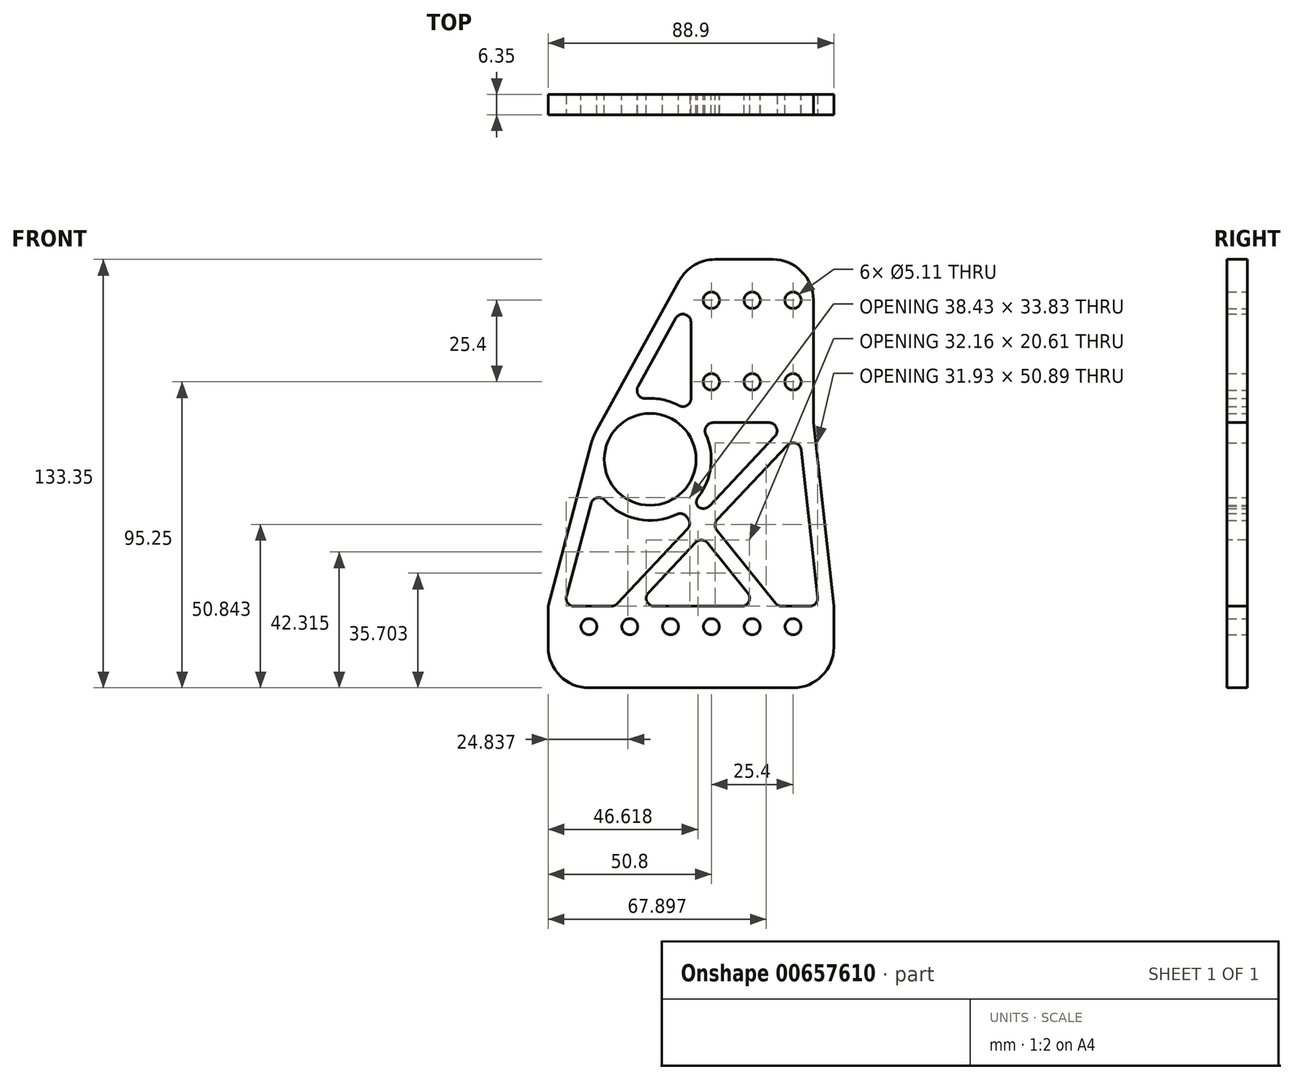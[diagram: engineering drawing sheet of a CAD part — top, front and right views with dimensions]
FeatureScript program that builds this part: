
annotation { "Feature Type Name" : "Feature", "Feature Type Description" : "" }
export const myFeature = defineFeature(function(context is Context, id is Id, definition is map)
    precondition{}
    {
        {
            var Q0;
            Q0=qCreatedBy(makeId("Front.planeOp"),FACE);
            var sketch = newSketch(context, id + "F0", { "sketchPlane" : qUnion([Q0])});
            skLineSegment(sketch, "E0.bottom", {"start": v(0, 0) * mm, "end": v(-88.9, 0) * mm});
            skLineSegment(sketch, "E0.top", {"start": v(0, -152.4) * mm, "end": v(-88.9, -152.4) * mm});
            skLineSegment(sketch, "E0.left", {"start": v(0, 0) * mm, "end": v(0, -152.4) * mm});
            skLineSegment(sketch, "E0.right", {"start": v(-88.9, 0) * mm, "end": v(-88.9, -152.4) * mm});
            skCircle(sketch, "E1", {"center": v(-12.7, -31.75) * mm, "radius": 2.55 * mm});
            skCircle(sketch, "E2", {"center": v(-57.15, -81.28) * mm, "radius": 14.29 * mm});
            skCircle(sketch, "E3.0.1.0", {"center": v(-12.7, -57.15) * mm, "radius": 2.55 * mm});
            skCircle(sketch, "E3.1.0.0", {"center": v(-25.4, -31.75) * mm, "radius": 2.55 * mm});
            skCircle(sketch, "E3.1.1.0", {"center": v(-25.4, -57.15) * mm, "radius": 2.55 * mm});
            skCircle(sketch, "E3.2.0.0", {"center": v(-38.1, -31.75) * mm, "radius": 2.55 * mm});
            skCircle(sketch, "E3.2.1.0", {"center": v(-38.1, -57.15) * mm, "radius": 2.55 * mm});
            skLineSegment(sketch, "E3.direction1", {"start": v(-12.7, -31.75) * mm, "end": v(-25.4, -31.75) * mm, "construction": true});
            skLineSegment(sketch, "E3.direction2", {"start": v(-12.7, -31.75) * mm, "end": v(-12.7, -57.15) * mm, "construction": true});
            skCircle(sketch, "E4", {"center": v(-57.15, -81.28) * mm, "radius": 18.99 * mm});
            skLineSegment(sketch, "E5", {"start": v(-88.9, -127) * mm, "end": v(0, -127) * mm});
            skLineSegment(sketch, "E6", {"start": v(-88.9, -127) * mm, "end": v(-75.5, -76.42) * mm});
            skLineSegment(sketch, "E7", {"start": v(-74.16, -89.7) * mm, "end": v(-84.04, -127) * mm});
            skLineSegment(sketch, "E8", {"start": v(0, -19.05) * mm, "end": v(-44.45, -19.05) * mm});
            skLineSegment(sketch, "E9", {"start": v(-44.45, -19.05) * mm, "end": v(-44.45, -69.85) * mm});
            skLineSegment(sketch, "E10", {"start": v(-44.45, -69.85) * mm, "end": v(0, -69.85) * mm});
            skPoint(sketch, "E11", {"position": v(-25.4, -44.45) * mm});
            skLineSegment(sketch, "E12", {"start": v(-44.45, -19.05) * mm, "end": v(-73.77, -72.1) * mm});
            skLineSegment(sketch, "E13", {"start": v(-44.45, -28.76) * mm, "end": v(-63.6, -63.42) * mm});
            skLineSegment(sketch, "E14", {"start": v(-6.35, -19.05) * mm, "end": v(-6.35, -69.85) * mm});
            skLineSegment(sketch, "E15", {"start": v(-6.35, -69.85) * mm, "end": v(0, -127) * mm});
            skLineSegment(sketch, "E16", {"start": v(-4.73, -127) * mm, "end": v(-11.08, -69.85) * mm});
            skLineSegment(sketch, "E17", {"start": v(-57.15, -81.28) * mm, "end": v(-25.4, -44.45) * mm, "construction": true});
            skLineSegment(sketch, "E18", {"start": v(-46.63, -65.48) * mm, "end": v(-44.45, -62.95) * mm});
            skLineSegment(sketch, "E19", {"start": v(-44.45, -70.15) * mm, "end": v(-43.07, -68.54) * mm});
            skLineSegment(sketch, "E20", {"start": v(-57.15, -81.28) * mm, "end": v(0, -152.4) * mm, "construction": true});
            skLineSegment(sketch, "E21", {"start": v(-47.18, -97.44) * mm, "end": v(-43.52, -94.5) * mm, "construction": true});
            skLineSegment(sketch, "E22", {"start": v(-43.52, -94.5) * mm, "end": v(-17.4, -127) * mm});
            skLineSegment(sketch, "E23", {"start": v(-47.18, -97.44) * mm, "end": v(-23.42, -127) * mm});
            skLineSegment(sketch, "E24", {"start": v(-88.9, -152.4) * mm, "end": v(-11.08, -69.85) * mm, "construction": true});
            skLineSegment(sketch, "E25", {"start": v(-61.73, -127) * mm, "end": v(-10.74, -72.91) * mm});
            skLineSegment(sketch, "E26", {"start": v(-14.3, -69.85) * mm, "end": v(-68.18, -127) * mm});
            skCircle(sketch, "E27", {"center": v(-76.2, -133.35) * mm, "radius": 2.49 * mm});
            skCircle(sketch, "E28.1.0.0", {"center": v(-63.5, -133.35) * mm, "radius": 2.49 * mm});
            skCircle(sketch, "E28.2.0.0", {"center": v(-50.8, -133.35) * mm, "radius": 2.49 * mm});
            skCircle(sketch, "E28.3.0.0", {"center": v(-38.1, -133.35) * mm, "radius": 2.49 * mm});
            skCircle(sketch, "E28.4.0.0", {"center": v(-25.4, -133.35) * mm, "radius": 2.49 * mm});
            skCircle(sketch, "E28.5.0.0", {"center": v(-12.7, -133.35) * mm, "radius": 2.49 * mm});
            skLineSegment(sketch, "E28.direction1", {"start": v(-76.2, -133.35) * mm, "end": v(-63.5, -133.35) * mm, "construction": true});
            skSolve(sketch);
        }
        {
            var Q0;
            Q0=makeQuery(id+"F0.imprint","IMPRINT",FACE,{"disambiguationData":[TD([[makeQuery(id+"F0.imprint","IMPRINT",EDGE,{"derivedFrom":sQuery(id+"F0.wireOp",EDGE,"E2")}),-1.0]])]});
            var Q1;
            {var subQ0=sQuery(id+"F0.wireOp",EDGE,"E12");Q1=makeQuery(id+"F0.imprint","IMPRINT",FACE,{"disambiguationData":[TD([[makeQuery(id+"F0.imprint","IMPRINT",EDGE,{"derivedFrom":subQ0}),1.0]])]});}
            var Q2;
            {var subQ0=sQuery(id+"F0.wireOp",EDGE,"E6");Q2=makeQuery(id+"F0.imprint","IMPRINT",FACE,{"disambiguationData":[TD([[makeQuery(id+"F0.imprint","IMPRINT",EDGE,{"derivedFrom":subQ0}),-1.0]])]});}
            var Q3;
            {var subQ4=sQuery(id+"F0.wireOp",EDGE,"E0.top");Q3=makeQuery(id+"F0.imprint","IMPRINT",FACE,{"disambiguationData":[TD([[makeQuery(id+"F0.imprint","IMPRINT",EDGE,{"derivedFrom":subQ4}),-1.0]])]});}
            var Q4;
            {var subQ0=sQuery(id+"F0.wireOp",EDGE,"E15");Q4=makeQuery(id+"F0.imprint","IMPRINT",FACE,{"disambiguationData":[TD([[makeQuery(id+"F0.imprint","IMPRINT",EDGE,{"derivedFrom":subQ0}),-1.0]])]});}
            var Q5;
            Q5=makeQuery(id+"F0.imprint","IMPRINT",FACE,{"disambiguationData":[TD([[makeQuery(id+"F0.imprint","IMPRINT",EDGE,{"derivedFrom":sQuery(id+"F0.wireOp",EDGE,"E1")}),-1.0]])]});
            var Q6;
            {var subQ0=sQuery(id+"F0.wireOp",EDGE,"E25");var subQ1=sQuery(id+"F0.wireOp",EDGE,"E5");var subQ2=makeQuery(id+"F0.imprint","INTERSECT",VERTEX,{"derivedFrom":[subQ1,subQ0]});Q6=makeQuery(id+"F0.imprint","IMPRINT",FACE,{"disambiguationData":[TD([[makeQuery(id+"F0.imprint","IMPRINT",EDGE,{"disambiguationData":[TD([[subQ2,1.0]])],"derivedFrom":subQ1}),1.0]])]});}
            var Q7;
            {var subQ0=sQuery(id+"F0.wireOp",EDGE,"E26");var subQ1=sQuery(id+"F0.wireOp",EDGE,"E22");var subQ2=makeQuery(id+"F0.imprint","INTERSECT",VERTEX,{"derivedFrom":[subQ1,subQ0]});Q7=makeQuery(id+"F0.imprint","IMPRINT",FACE,{"disambiguationData":[TD([[makeQuery(id+"F0.imprint","IMPRINT",EDGE,{"disambiguationData":[TD([[subQ2,-1.0]])],"derivedFrom":subQ1}),-1.0]])]});}
            var Q8;
            {var subQ1=sQuery(id+"F0.wireOp",EDGE,"E16");var subQ5=sQuery(id+"F0.wireOp",EDGE,"E10");var subQ6=makeQuery(id+"F0.imprint","INTERSECT",VERTEX,{"derivedFrom":[subQ5,subQ1]});Q8=makeQuery(id+"F0.imprint","IMPRINT",FACE,{"disambiguationData":[TD([[makeQuery(id+"F0.imprint","IMPRINT",EDGE,{"disambiguationData":[TD([[subQ6,1.0]])],"derivedFrom":subQ5}),-1.0]])]});}
            var Q9;
            {var subQ0=sQuery(id+"F0.wireOp",EDGE,"E22");var subQ1=sQuery(id+"F0.wireOp",EDGE,"E4");var subQ2=makeQuery(id+"F0.imprint","INTERSECT",VERTEX,{"derivedFrom":[subQ1,subQ0]});Q9=makeQuery(id+"F0.imprint","IMPRINT",FACE,{"disambiguationData":[TD([[makeQuery(id+"F0.imprint","IMPRINT",EDGE,{"disambiguationData":[TD([[subQ2,1.0]])],"derivedFrom":subQ1}),-1.0]])]});}
            var Q10;
            {var subQ0=sQuery(id+"F0.wireOp",EDGE,"E22");var subQ1=sQuery(id+"F0.wireOp",EDGE,"E5");var subQ2=makeQuery(id+"F0.imprint","INTERSECT",VERTEX,{"derivedFrom":[subQ1,subQ0]});Q10=makeQuery(id+"F0.imprint","IMPRINT",FACE,{"disambiguationData":[TD([[makeQuery(id+"F0.imprint","IMPRINT",EDGE,{"disambiguationData":[TD([[subQ2,1.0]])],"derivedFrom":subQ1}),1.0]])]});}
            var Q11;
            {var subQ0=sQuery(id+"F0.wireOp",EDGE,"E19");var subQ1=sQuery(id+"F0.wireOp",EDGE,"E4");var subQ2=makeQuery(id+"F0.imprint","INTERSECT",VERTEX,{"derivedFrom":[subQ1,subQ0]});Q11=makeQuery(id+"F0.imprint","IMPRINT",FACE,{"disambiguationData":[TD([[makeQuery(id+"F0.imprint","IMPRINT",EDGE,{"disambiguationData":[TD([[subQ2,-1.0]])],"derivedFrom":subQ1}),1.0]])]});}
            var Q12;
            {var subQ0=sQuery(id+"F0.wireOp",EDGE,"E19");var subQ1=sQuery(id+"F0.wireOp",EDGE,"E4");var subQ2=makeQuery(id+"F0.imprint","INTERSECT",VERTEX,{"derivedFrom":[subQ1,subQ0]});Q12=makeQuery(id+"F0.imprint","IMPRINT",FACE,{"disambiguationData":[TD([[makeQuery(id+"F0.imprint","IMPRINT",EDGE,{"disambiguationData":[TD([[subQ2,1.0]])],"derivedFrom":subQ1}),1.0]])]});}
            extrude(context, id + "F1", {"entities" : qUnion([Q0, Q1, Q2, Q3, Q4, Q5, Q6, Q7, Q8, Q9, Q10, Q11, Q12]), "depth" : 6.35 * mm, "offsetDistance" : 25.4 * mm});
        }
        {
            var Q0;
            Q0=makeQuery(id+"F1.opExtrude","SWEPT_EDGE",EDGE,{"disambiguationData":[OSD([sQuery(id+"F0.wireOp",EDGE,"E8"),sQuery(id+"F0.wireOp",EDGE,"E14")])]});
            var Q1;
            Q1=makeQuery(id+"F1.opExtrude","SWEPT_EDGE",EDGE,{"disambiguationData":[OSD([sQuery(id+"F0.wireOp",EDGE,"E0.top"),sQuery(id+"F0.wireOp",EDGE,"E0.right")])]});
            var Q2;
            Q2=makeQuery(id+"F1.opExtrude","SWEPT_EDGE",EDGE,{"disambiguationData":[OSD([sQuery(id+"F0.wireOp",EDGE,"E0.top"),sQuery(id+"F0.wireOp",EDGE,"E0.left")])]});
            var Q3;
            Q3=makeQuery(id+"F1.opExtrude","SWEPT_EDGE",EDGE,{"disambiguationData":[OSD([sQuery(id+"F0.wireOp",EDGE,"E8"),sQuery(id+"F0.wireOp",EDGE,"E9"),sQuery(id+"F0.wireOp",EDGE,"E12")])]});
            fillet(context, id + "F2", {"entities" : qUnion([Q0, Q1, Q2, Q3]), "tangentPropagation" : true, "radius" : 12.7 * mm, "defaultsChanged" : false, "vertexSettings" : [], "allowEdgeOverflow" : false});
        }
        {
            var Q0;
            Q0=makeQuery(id+"F1.opExtrude","SWEPT_EDGE",EDGE,{"disambiguationData":[OSD([sQuery(id+"F0.wireOp",EDGE,"E4"),sQuery(id+"F0.wireOp",EDGE,"E19")])]});
            var Q1;
            Q1=makeQuery(id+"F1.opExtrude","SWEPT_EDGE",EDGE,{"disambiguationData":[OSD([sQuery(id+"F0.wireOp",EDGE,"E9"),sQuery(id+"F0.wireOp",EDGE,"E19")])]});
            var Q2;
            Q2=makeQuery(id+"F1.opExtrude","SWEPT_EDGE",EDGE,{"disambiguationData":[OSD([sQuery(id+"F0.wireOp",EDGE,"E4"),sQuery(id+"F0.wireOp",EDGE,"E23")])]});
            var Q3;
            Q3=makeQuery(id+"F1.opExtrude","SWEPT_EDGE",EDGE,{"disambiguationData":[OSD([sQuery(id+"F0.wireOp",EDGE,"E4"),sQuery(id+"F0.wireOp",EDGE,"E7")])]});
            var Q4;
            Q4=makeQuery(id+"F1.opExtrude","SWEPT_EDGE",EDGE,{"disambiguationData":[OSD([sQuery(id+"F0.wireOp",EDGE,"E9"),sQuery(id+"F0.wireOp",EDGE,"E13")])]});
            var Q5;
            Q5=makeQuery(id+"F1.opExtrude","SWEPT_EDGE",EDGE,{"disambiguationData":[OSD([sQuery(id+"F0.wireOp",EDGE,"E4"),sQuery(id+"F0.wireOp",EDGE,"E13")])]});
            var Q6;
            Q6=makeQuery(id+"F1.opExtrude","SWEPT_EDGE",EDGE,{"disambiguationData":[OSD([sQuery(id+"F0.wireOp",EDGE,"E9"),sQuery(id+"F0.wireOp",EDGE,"E18")])]});
            var Q7;
            Q7=makeQuery(id+"F1.opExtrude","SWEPT_EDGE",EDGE,{"disambiguationData":[OSD([sQuery(id+"F0.wireOp",EDGE,"E4"),sQuery(id+"F0.wireOp",EDGE,"E18")])]});
            var Q8;
            Q8=makeQuery(id+"F1.opExtrude","SWEPT_EDGE",EDGE,{"disambiguationData":[OSD([sQuery(id+"F0.wireOp",EDGE,"E22"),sQuery(id+"F0.wireOp",EDGE,"E26")])]});
            var Q9;
            Q9=makeQuery(id+"F1.opExtrude","SWEPT_EDGE",EDGE,{"disambiguationData":[OSD([sQuery(id+"F0.wireOp",EDGE,"E5"),sQuery(id+"F0.wireOp",EDGE,"E26")])]});
            var Q10;
            Q10=makeQuery(id+"F1.opExtrude","SWEPT_EDGE",EDGE,{"disambiguationData":[OSD([sQuery(id+"F0.wireOp",EDGE,"E5"),sQuery(id+"F0.wireOp",EDGE,"E7")])]});
            var Q11;
            Q11=makeQuery(id+"F1.opExtrude","SWEPT_EDGE",EDGE,{"disambiguationData":[OSD([sQuery(id+"F0.wireOp",EDGE,"E9"),sQuery(id+"F0.wireOp",EDGE,"E10")])]});
            var Q12;
            Q12=makeQuery(id+"F1.opExtrude","SWEPT_EDGE",EDGE,{"disambiguationData":[OSD([sQuery(id+"F0.wireOp",EDGE,"E10"),sQuery(id+"F0.wireOp",EDGE,"E26")])]});
            var Q13;
            Q13=makeQuery(id+"F1.opExtrude","SWEPT_EDGE",EDGE,{"disambiguationData":[OSD([sQuery(id+"F0.wireOp",EDGE,"E23"),sQuery(id+"F0.wireOp",EDGE,"E26")])]});
            var Q14;
            Q14=makeQuery(id+"F1.opExtrude","SWEPT_EDGE",EDGE,{"disambiguationData":[OSD([sQuery(id+"F0.wireOp",EDGE,"E23"),sQuery(id+"F0.wireOp",EDGE,"E25")])]});
            var Q15;
            Q15=makeQuery(id+"F1.opExtrude","SWEPT_EDGE",EDGE,{"disambiguationData":[OSD([sQuery(id+"F0.wireOp",EDGE,"E22"),sQuery(id+"F0.wireOp",EDGE,"E25")])]});
            var Q16;
            Q16=makeQuery(id+"F1.opExtrude","SWEPT_EDGE",EDGE,{"disambiguationData":[OSD([sQuery(id+"F0.wireOp",EDGE,"E5"),sQuery(id+"F0.wireOp",EDGE,"E25")])]});
            var Q17;
            Q17=makeQuery(id+"F1.opExtrude","SWEPT_EDGE",EDGE,{"disambiguationData":[OSD([sQuery(id+"F0.wireOp",EDGE,"E5"),sQuery(id+"F0.wireOp",EDGE,"E23")])]});
            var Q18;
            Q18=makeQuery(id+"F1.opExtrude","SWEPT_EDGE",EDGE,{"disambiguationData":[OSD([sQuery(id+"F0.wireOp",EDGE,"E5"),sQuery(id+"F0.wireOp",EDGE,"E16")])]});
            var Q19;
            Q19=makeQuery(id+"F1.opExtrude","SWEPT_EDGE",EDGE,{"disambiguationData":[OSD([sQuery(id+"F0.wireOp",EDGE,"E16"),sQuery(id+"F0.wireOp",EDGE,"E25")])]});
            var Q20;
            Q20=makeQuery(id+"F1.opExtrude","SWEPT_EDGE",EDGE,{"disambiguationData":[OSD([sQuery(id+"F0.wireOp",EDGE,"E5"),sQuery(id+"F0.wireOp",EDGE,"E22")])]});
            fillet(context, id + "F3", {"entities" : qUnion([Q0, Q1, Q2, Q3, Q4, Q5, Q6, Q7, Q8, Q9, Q10, Q11, Q12, Q13, Q14, Q15, Q16, Q17, Q18, Q19, Q20]), "tangentPropagation" : true, "radius" : 2.54 * mm, "defaultsChanged" : true, "vertexSettings" : [], "allowEdgeOverflow" : false});
        }
    });
